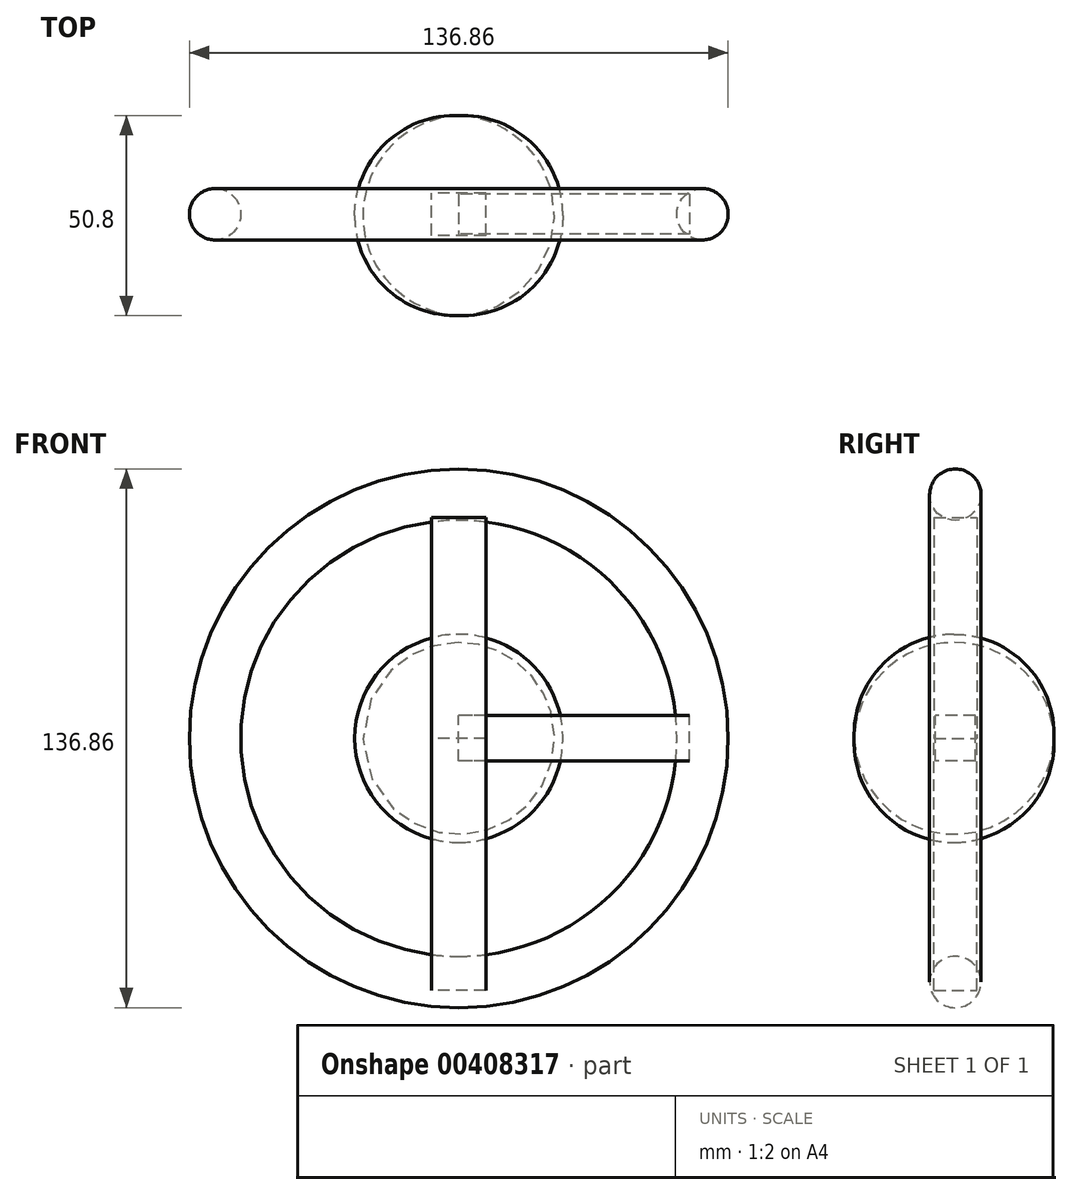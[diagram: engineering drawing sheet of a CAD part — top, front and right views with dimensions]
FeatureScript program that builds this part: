
annotation { "Feature Type Name" : "Feature", "Feature Type Description" : "" }
export const myFeature = defineFeature(function(context is Context, id is Id, definition is map)
    precondition{}
    {
        {
            var Q0;
            Q0=qCreatedBy(makeId("Top.planeOp"),FACE);
            var sketch = newSketch(context, id + "F0", { "sketchPlane" : qUnion([Q0])});
            skArc(sketch, "E0", {"start": v(0, 25.05) * mm, "mid": v(-26.44, -0.33) * mm, "end": v(0, -25.7) * mm});
            skLineSegment(sketch, "E1", {"start": v(0, -25.7) * mm, "end": v(0, 25.05) * mm});
            skSolve(sketch);
        }
        {
            var Q0;
            Q0 = qSketchRegion(id + "F0", true);
            var Q1;
            Q1=sQuery(id+"F0.wireOp",EDGE,"E1");
            revolve(context, id + "F1", {"entities" : qUnion([Q0]), "axis" : qUnion([Q1]), "revolveType" : RevolveType.FULL});
        }
        {
            var Q0;
            Q0=qCreatedBy(makeId("Top.planeOp"),FACE);
            var sketch = newSketch(context, id + "F2", { "sketchPlane" : qUnion([Q0])});
            skCircle(sketch, "E2", {"center": v(-61.9, 0) * mm, "radius": 6.53 * mm});
            skSolve(sketch);
        }
        {
            var Q0;
            Q0=qCreatedBy(makeId("Front.planeOp"),FACE);
            var sketch = newSketch(context, id + "F3", { "sketchPlane" : qUnion([Q0])});
            skCircle(sketch, "E3", {"center": v(0, 0) * mm, "radius": 57.47 * mm});
            skSolve(sketch);
        }
        {
            var Q0;
            Q0=makeQuery(id+"F2.imprint","IMPRINT",FACE,{"disambiguationData":[TD([[makeQuery(id+"F2.imprint","IMPRINT",EDGE,{"derivedFrom":sQuery(id+"F2.wireOp",EDGE,"E2")}),1.0]])]});
            var Q1;
            Q1=sQuery(id+"F3.wireOp",EDGE,"E3");
            sweep(context, id + "F4", {"profiles" : qUnion([Q0]), "path" : qUnion([Q1])});
        }
        {
            var Q0;
            Q0=qCreatedBy(makeId("Top.planeOp"),FACE);
            var sketch = newSketch(context, id + "F5", { "sketchPlane" : qUnion([Q0])});
            skLineSegment(sketch, "E4.bottom", {"start": v(6.88, -5.43) * mm, "end": v(-6.88, -5.43) * mm});
            skLineSegment(sketch, "E4.top", {"start": v(6.88, 5.43) * mm, "end": v(-6.88, 5.43) * mm});
            skLineSegment(sketch, "E4.left", {"start": v(6.88, -5.43) * mm, "end": v(6.88, 5.43) * mm});
            skLineSegment(sketch, "E4.right", {"start": v(-6.88, -5.43) * mm, "end": v(-6.88, 5.43) * mm});
            skPoint(sketch, "E4.middle", {"position": v(0, 0) * mm});
            skSolve(sketch);
        }
        {
            var Q0;
            Q0 = qSketchRegion(id + "F5", true);
            extrude(context, id + "F6", {"entities" : qUnion([Q0]), "depth" : 56.13 * mm});
        }
        {
            var Q0;
            Q0 = qSketchRegion(id + "F5", true);
            extrude(context, id + "F7", {"entities" : qUnion([Q0]), "oppositeDirection" : true, "depth" : 64 * mm});
        }
        {
            var Q0;
            Q0=qCreatedBy(makeId("Right.planeOp"),FACE);
            var sketch = newSketch(context, id + "F8", { "sketchPlane" : qUnion([Q0])});
            skLineSegment(sketch, "E5.bottom", {"start": v(5.07, -5.8) * mm, "end": v(-5.07, -5.8) * mm});
            skLineSegment(sketch, "E5.top", {"start": v(5.07, 5.8) * mm, "end": v(-5.07, 5.8) * mm});
            skLineSegment(sketch, "E5.left", {"start": v(5.07, -5.8) * mm, "end": v(5.07, 5.8) * mm});
            skLineSegment(sketch, "E5.right", {"start": v(-5.07, -5.8) * mm, "end": v(-5.07, 5.8) * mm});
            skPoint(sketch, "E5.middle", {"position": v(0, 0) * mm});
            skSolve(sketch);
        }
        {
            var Q0;
            Q0 = qSketchRegion(id + "F8", true);
            extrude(context, id + "F9", {"entities" : qUnion([Q0]), "depth" : 58.67 * mm});
        }
    });
